# Revit family: rba-bim-rba2733-032
name_source: partatom
category: Plumbing Fixtures
revit_build: Autodesk Revit 2015 (Build: 20140223_1515(x64)
units: mm (PartAtom-declared; Revit-internal decimal feet)

## types (2) — shared parameters
AA111400S-FG = Yes
Amperage = 4
CW Connection = Yes
HW Connection = No
Manufacturer = RBA Group
Material = Stainless Steel
SIZE  WIDTH = 18.5
SIZE DEPTH = 18.5
SIZE LENGTH = 20.5
Tempered Water Connection = No
URL = http://www.rba.com.au
Vent Connection = No
Voltage = 110
Waste Connection = Yes
zero-valued in all types: Default Elevation

## per-type parameters (varying)
| type | Description | Modified Issue |
| RBA2733-032 | Compact Wall Mount - Water Cooler, Stainless Steel 1.6mm | 20161010.01 |
| RBA2733-132 | Compact Wall Mount - Water Cooler, Stainless Steel 1.6mm, with glass filler | 20160816.01 |

note: column(s) folded — value = type name in every type: Model

## geometry (parser evidence)
native form markers: Blend x16, Sweep x8
no freeform markers — native parametric forms only
